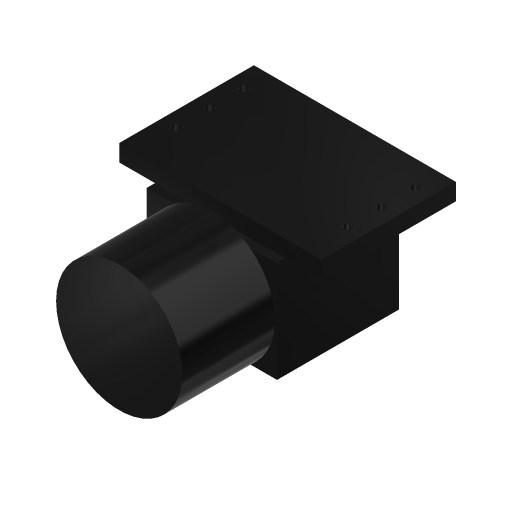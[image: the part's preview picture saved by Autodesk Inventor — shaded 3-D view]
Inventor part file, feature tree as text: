
AUTODESK INVENTOR PART (.ipt)
format: ipt  version: 2024.1 (Build 281209000, 209)  size: 166,912 bytes
history: native  units: mm
features: extrude x5, sketch x5, projected_geometry x3
ambient origin geometry x8: Origin, YZ Plane, XZ Plane, XY Plane, X Axis, Y Axis, Z Axis, Center Point
bodies: Volumenkörper1 (feature_tree)
feature tree (13):
  extrude  "Extrusion1"  Depth=14.5mm
  extrude  "Extrusion2"  Depth=24.0mm
  extrude  "Extrusion3"  Depth=2.5mm
  extrude  "Extrusion4"  Depth=2.0mm
  extrude  "Extrusion5"  Depth=7.0mm TaperAngle=0.0deg
  sketch  "Skizze1"  dims[d0=15.5mm d1=14.5mm]
  sketch  "Skizze2"  dims[d2=12.0mm d3=0.0mm d4=24.0mm]
  sketch  "Skizze3"  dims[d5=16.0mm d6=2.5mm]
  projected_geometry  "Projizierte Kontur1"
  sketch  "Skizze4"  dims[d7=2.0mm d8=0.0mm d9=3.0mm]
  projected_geometry  "Projizierte Kontur2"
  sketch  "Skizze5"  dims[d10=1.124503mm d11=7.0mm d12=0.0mm d13=15.0mm d14=11.0mm d15=0.0mm d16=1.0mm d17=1.0mm d18=1.0mm d19=5.0mm d20=4.0mm d21=4.0mm d22=1.8mm d23=1.8mm d24=1.8mm d25=11.0mm d26=0.0mm]
  projected_geometry  "Projizierte Kontur3"
